# Revit family: WALL WASHER HIGH POWER LED RGB 100CM_LK2036RGB.30
name_source: partatom
category: Luminarias
units: mm (PartAtom-declared; Revit-internal decimal feet)

## family parameters
Compartido = No
Corte con vacíos al cargar = No
Cota de conector redondo = Diámetro de uso
Origen de luz = Sí
Punto de cálculo de habitación = No
Se basa en plano de trabajo = Sí
Siempre vertical = No
Tipo de pieza = Normal

## types (1)
- REFL_LK2036RGB.30
    Archivo de red fotométrica = LK2036RGB.IES
    Cambio de temperatura de color de luz atenuada = Curva de lámpara incandescente
    Comentarios de vataje = 24V
    Descripción = LUMINARIA TIPO REFLECTOR LINEAL, WALL WASHER , CUERPO DE ALUMINIO EXTRUIDO CON POLVO GRIS, VIDRIO TEMPLADO DE 3MM ADEMAS DEL SELLADO CON SILICON EN VIDRIO Y HOUSING, CUENTA CON 20 LED TIPO OSRAM CON UN CONSUMO TOTAL DE 67.2W, 1386 LUMENES, RGB, IP 66, IK 05, CABLE H05RN DE 0.5M, APERTURA DE 30 GRADOS, ALIMENTADA A 24V. REQUIERE ACCESORIOS.
    Elevación por defecto = 0 mm  [stored 0 ft]
    Fabricante = BRILLANT
    Filtro de color = 16777215
    Longitud de línea de emisión = 400 mm  [stored 1.31234 ft]
    Lámpara = OSRAM
    Modelo = LK2036RGB.30
    Watt per fixture = 67.2
    Ángulo de inclinación = 60.00°

note: [stored X ft] marks values corroborated as IEEE doubles in the binary element streams (Revit-internal decimal feet)

## geometry (parser evidence)
native form markers: Blend x2
no freeform markers — native parametric forms only
